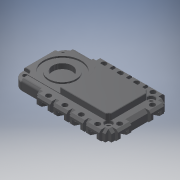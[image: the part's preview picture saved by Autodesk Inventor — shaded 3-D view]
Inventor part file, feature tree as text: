
AUTODESK INVENTOR PART (.ipt)
format: ipt  version: 2018 (Build 220112000, 112)  size: 520,192 bytes
history: native  units: mm
features: other x1, chamfer x1
ambient origin geometry x8: Origin, YZ Plane, XZ Plane, XY Plane, X Axis, Y Axis, Z Axis, Center Point
bodies: Body1 (feature_tree)
feature tree (2):
  other  "Твердое тело1"
  chamfer  "Chamfer3"  [1 undecoded]
note: 1 required parameter value undecoded (feature->parameter linkage not recoverable at this tier; creation-order binding heuristic only, values carry confidence <= 0.55)
